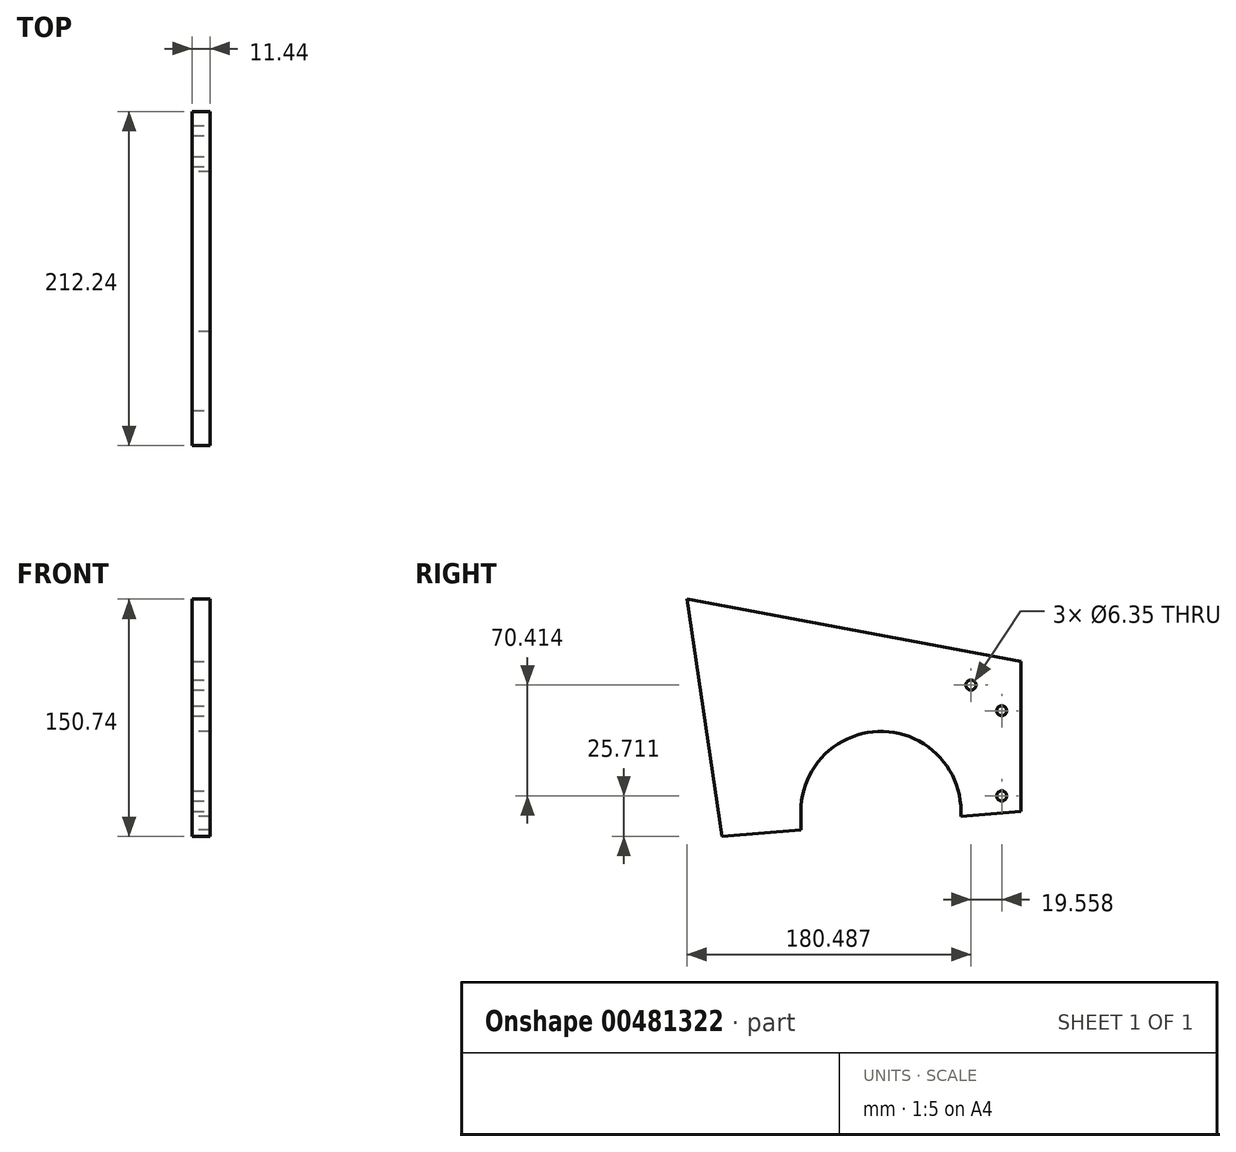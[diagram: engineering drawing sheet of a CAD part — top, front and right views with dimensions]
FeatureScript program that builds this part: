
annotation { "Feature Type Name" : "Feature", "Feature Type Description" : "" }
export const myFeature = defineFeature(function(context is Context, id is Id, definition is map)
    precondition{}
    {
        {
            var Q0;
            Q0=qCreatedBy(makeId("Right.planeOp"),FACE);
            var sketch = newSketch(context, id + "F0", { "sketchPlane" : qUnion([Q0])});
            skLineSegment(sketch, "E0", {"start": v(122.12, 51.37) * mm, "end": v(-90.12, 90.98) * mm});
            skLineSegment(sketch, "E1", {"start": v(-90.12, 90.98) * mm, "end": v(-67.72, -59.76) * mm});
            skLineSegment(sketch, "E2", {"start": v(122.12, 51.37) * mm, "end": v(122.12, -43.88) * mm});
            skLineSegment(sketch, "E3", {"start": v(-67.72, -59.76) * mm, "end": v(122.12, -43.88) * mm});
            skCircle(sketch, "E4", {"center": v(90.37, 36.36) * mm, "radius": 3.18 * mm});
            skCircle(sketch, "E5", {"center": v(109.92, 20.05) * mm, "radius": 3.18 * mm});
            skCircle(sketch, "E6", {"center": v(109.92, -34.05) * mm, "radius": 3.18 * mm});
            skSolve(sketch);
        }
        {
            var Q0;
            Q0=qSketchRegion(id+"F0",true);
            var Q1;
            Q1=makeQuery(id+"F0.imprint","IMPRINT",FACE,{"disambiguationData":[TD([[makeQuery(id+"F0.imprint","IMPRINT",EDGE,{"derivedFrom":sQuery(id+"F0.wireOp",EDGE,"E4")}),1.0]])]});
            var Q2;
            Q2=makeQuery(id+"F0.imprint","IMPRINT",FACE,{"disambiguationData":[TD([[makeQuery(id+"F0.imprint","IMPRINT",EDGE,{"derivedFrom":sQuery(id+"F0.wireOp",EDGE,"E5")}),1.0]])]});
            var Q3;
            Q3=makeQuery(id+"F0.imprint","IMPRINT",FACE,{"disambiguationData":[TD([[makeQuery(id+"F0.imprint","IMPRINT",EDGE,{"derivedFrom":sQuery(id+"F0.wireOp",EDGE,"E6")}),1.0]])]});
            extrude(context, id + "F1", {"entities" : qUnion([Q0, Q1, Q2, Q3]), "depth" : 11.43 * mm});
        }
        {
            var Q0;
            Q0=makeQuery(id+"F1.opExtrude","SWEPT_BODY",BODY,{"disambiguationData":[OSD([sQuery(id+"F0.wireOp",EDGE,"E0"),sQuery(id+"F0.wireOp",EDGE,"E1"),sQuery(id+"F0.wireOp",EDGE,"E2"),sQuery(id+"F0.wireOp",EDGE,"E3"),sQuery(id+"F0.wireOp",EDGE,"E4"),sQuery(id+"F0.wireOp",EDGE,"E5"),sQuery(id+"F0.wireOp",EDGE,"E6")])]});
            transform(context, id + "F2", {"entities" : qUnion([Q0]), "transformType" : TransformType.TRANSLATION_3D, "dx" : 47.62 * mm, "dy" : 0 * mm, "dz" : 0 * mm, "makeCopy" : false});
        }
        {
            var Q0;
            Q0=makeQuery(id+"F1.opExtrude","SWEPT_BODY",BODY,{"disambiguationData":[OSD([sQuery(id+"F0.wireOp",EDGE,"E0"),sQuery(id+"F0.wireOp",EDGE,"E1"),sQuery(id+"F0.wireOp",EDGE,"E2"),sQuery(id+"F0.wireOp",EDGE,"E3"),sQuery(id+"F0.wireOp",EDGE,"E4"),sQuery(id+"F0.wireOp",EDGE,"E5"),sQuery(id+"F0.wireOp",EDGE,"E6")])]});
            var Q1;
            Q1=qCreatedBy(makeId("Right.planeOp"),FACE);
            mirror(context, id + "F3", {"entities" : qUnion([Q0]), "mirrorPlane" : qUnion([Q1])});
        }
        {
            var Q0;
            Q0=makeQuery(id+"F3.opPattern","COPY",FACE,{"derivedFrom":makeQuery(id+"F1.opExtrude","CAP_FACE",FACE,{"disambiguationData":[OSD([sQuery(id+"F0.wireOp",EDGE,"E0"),sQuery(id+"F0.wireOp",EDGE,"E1"),sQuery(id+"F0.wireOp",EDGE,"E2"),sQuery(id+"F0.wireOp",EDGE,"E3"),sQuery(id+"F0.wireOp",EDGE,"E4"),sQuery(id+"F0.wireOp",EDGE,"E5"),sQuery(id+"F0.wireOp",EDGE,"E6")])],"isStart":false}),"instanceName":"1"});
            var sketch = newSketch(context, id + "F4", { "sketchPlane" : qUnion([Q0])});
            skLineSegment(sketch, "E7", {"start": v(-122.12, -43.88) * mm, "end": v(-33.22, -43.88) * mm});
            skCircle(sketch, "E8", {"center": v(-33.22, -43.88) * mm, "radius": 50.8 * mm});
            skLineSegment(sketch, "E9", {"start": v(17.58, -43.88) * mm, "end": v(17.58, -55.57) * mm});
            skSolve(sketch);
        }
        {
            var Q0;
            {var subQ0=sQuery(id+"F4.wireOp",EDGE,"E8");var subQ1=makeQuery(id+"F4.imprint","INTERSECT",VERTEX,{"derivedFrom":[subQ0,sQuery(id+"F4.wireOp",EDGE,"E9")]});Q0=makeQuery(id+"F4.imprint","IMPRINT",FACE,{"disambiguationData":[TD([[makeQuery(id+"F4.imprint","IMPRINT",EDGE,{"disambiguationData":[TD([[subQ1,-1.0]])],"derivedFrom":subQ0}),1.0]])]});}
            var Q1;
            {var subQ0=sQuery(id+"F4.wireOp",EDGE,"E9");Q1=makeQuery(id+"F4.imprint","IMPRINT",FACE,{"disambiguationData":[TD([[makeQuery(id+"F4.imprint","IMPRINT",EDGE,{"derivedFrom":subQ0}),-1.0]])]});}
            extrude(context, id + "F5", {"entities" : qUnion([Q0, Q1]), "operationType" : NewBodyOperationType.REMOVE, "oppositeDirection" : true, "depth" : 25.4 * mm});
        }
        {
            var Q0;
            Q0=sQuery(id+"F0.wireOp",VERTEX,"E4.center");
            var Q1;
            Q1=makeQuery(id+"F3.opPattern","COPY",BODY,{"derivedFrom":makeQuery(id+"F1.opExtrude","SWEPT_BODY",BODY,{"disambiguationData":[OSD([sQuery(id+"F0.wireOp",EDGE,"E0"),sQuery(id+"F0.wireOp",EDGE,"E1"),sQuery(id+"F0.wireOp",EDGE,"E2"),sQuery(id+"F0.wireOp",EDGE,"E3")])]}),"instanceName":"1"});
            hole(context, id + "F6", {"style" : HoleStyle.SIMPLE, "endStyle" : HoleEndStyle.BLIND, "holeDiameter" : 6.35 * mm, "holeDepth" : 76.2 * mm, "isTappedThrough" : true, "tappedDepth" : 12.7 * mm, "tapClearance" : 3, "startFromSketch" : true, "locations" : qUnion([Q0]), "scope" : qUnion([Q1])});
        }
        {
            var Q0;
            Q0=sQuery(id+"F0.wireOp",VERTEX,"E5.center");
            var Q1;
            Q1=makeQuery(id+"F3.opPattern","COPY",BODY,{"derivedFrom":makeQuery(id+"F1.opExtrude","SWEPT_BODY",BODY,{"disambiguationData":[OSD([sQuery(id+"F0.wireOp",EDGE,"E0"),sQuery(id+"F0.wireOp",EDGE,"E1"),sQuery(id+"F0.wireOp",EDGE,"E2"),sQuery(id+"F0.wireOp",EDGE,"E3")])]}),"instanceName":"1"});
            hole(context, id + "F7", {"style" : HoleStyle.SIMPLE, "endStyle" : HoleEndStyle.BLIND, "holeDiameter" : 6.35 * mm, "holeDepth" : 76.2 * mm, "isTappedThrough" : true, "tappedDepth" : 12.7 * mm, "tapClearance" : 3, "startFromSketch" : true, "locations" : qUnion([Q0]), "scope" : qUnion([Q1])});
        }
        {
            var Q0;
            Q0=sQuery(id+"F0.wireOp",VERTEX,"E6.center");
            var Q1;
            Q1=makeQuery(id+"F3.opPattern","COPY",BODY,{"derivedFrom":makeQuery(id+"F1.opExtrude","SWEPT_BODY",BODY,{"disambiguationData":[OSD([sQuery(id+"F0.wireOp",EDGE,"E0"),sQuery(id+"F0.wireOp",EDGE,"E1"),sQuery(id+"F0.wireOp",EDGE,"E2"),sQuery(id+"F0.wireOp",EDGE,"E3")])]}),"instanceName":"1"});
            hole(context, id + "F8", {"style" : HoleStyle.SIMPLE, "endStyle" : HoleEndStyle.BLIND, "holeDiameter" : 6.35 * mm, "holeDepth" : 76.2 * mm, "isTappedThrough" : true, "tappedDepth" : 12.7 * mm, "tapClearance" : 3, "startFromSketch" : true, "locations" : qUnion([Q0]), "scope" : qUnion([Q1])});
        }
        {
            var Q0;
            Q0=sQuery(id+"F0.wireOp",VERTEX,"E4.center");
            var Q1;
            Q1=makeQuery(id+"F1.opExtrude","SWEPT_BODY",BODY,{"disambiguationData":[OSD([sQuery(id+"F0.wireOp",EDGE,"E0"),sQuery(id+"F0.wireOp",EDGE,"E1"),sQuery(id+"F0.wireOp",EDGE,"E2"),sQuery(id+"F0.wireOp",EDGE,"E3")])]});
            hole(context, id + "F9", {"style" : HoleStyle.SIMPLE, "endStyle" : HoleEndStyle.BLIND, "oppositeDirection" : true, "holeDiameter" : 6.35 * mm, "holeDepth" : 76.2 * mm, "isTappedThrough" : true, "tappedDepth" : 12.7 * mm, "tapClearance" : 3, "startFromSketch" : true, "locations" : qUnion([Q0]), "scope" : qUnion([Q1])});
        }
        {
            var Q0;
            Q0=makeQuery(id+"F1.opExtrude","CAP_FACE",FACE,{"disambiguationData":[OSD([sQuery(id+"F0.wireOp",EDGE,"E0"),sQuery(id+"F0.wireOp",EDGE,"E1"),sQuery(id+"F0.wireOp",EDGE,"E2"),sQuery(id+"F0.wireOp",EDGE,"E3")])],"isStart":true});
            var sketch = newSketch(context, id + "F10", { "sketchPlane" : qUnion([Q0])});
            skCircle(sketch, "E10", {"center": v(-90.37, 36.36) * mm, "radius": 66.68 * mm});
            skCircle(sketch, "E11.0", {"center": v(-90.37, 36.36) * mm, "radius": 161.93 * mm});
            skCircle(sketch, "E12.0", {"center": v(-90.37, 36.36) * mm, "radius": 164.47 * mm});
            skLineSegment(sketch, "E13", {"start": v(52.96, -38.98) * mm, "end": v(55.23, -40.13) * mm});
            skLineSegment(sketch, "E14", {"start": v(66.26, 86.53) * mm, "end": v(48.44, 142.17) * mm});
            skLineSegment(sketch, "E15", {"start": v(48.44, 142.17) * mm, "end": v(46.02, 141.4) * mm});
            skLineSegment(sketch, "E16", {"start": v(46.02, 141.4) * mm, "end": v(63.74, 86.06) * mm});
            skSolve(sketch);
        }
        {
            var Q0;
            {var subQ0=sQuery(id+"F10.wireOp",EDGE,"E14");Q0=makeQuery(id+"F10.imprint","IMPRINT",FACE,{"disambiguationData":[TD([[makeQuery(id+"F10.imprint","IMPRINT",EDGE,{"derivedFrom":subQ0}),1.0]])]});}
            var Q1;
            {var subQ1=makeQuery(id+"F1.opExtrude","CAP_EDGE",EDGE,{"disambiguationData":[OSD([sQuery(id+"F0.wireOp",EDGE,"E0")])],"isStart":true});var subQ3=sQuery(id+"F10.wireOp",EDGE,"E16");var subQ5=makeQuery(id+"F10.imprint","INTERSECT",VERTEX,{"derivedFrom":[subQ1,subQ3]});Q1=makeQuery(id+"F10.imprint","IMPRINT",FACE,{"disambiguationData":[TD([[makeQuery(id+"F10.imprint","IMPRINT",EDGE,{"disambiguationData":[TD([[subQ5,1.0]])],"derivedFrom":subQ3}),1.0]])]});}
            var Q2;
            {var subQ4=sQuery(id+"F10.wireOp",EDGE,"E13");Q2=makeQuery(id+"F10.imprint","IMPRINT",FACE,{"disambiguationData":[TD([[makeQuery(id+"F10.imprint","IMPRINT",EDGE,{"derivedFrom":subQ4}),1.0]])]});}
            extrude(context, id + "F11", {"entities" : qUnion([Q0, Q1, Q2]), "depth" : 95.25 * mm});
        }
        {
            var Q0;
            Q0=makeQuery(id+"F1.opExtrude","SWEPT_BODY",BODY,{"disambiguationData":[OSD([sQuery(id+"F0.wireOp",EDGE,"E0"),sQuery(id+"F0.wireOp",EDGE,"E1"),sQuery(id+"F0.wireOp",EDGE,"E2"),sQuery(id+"F0.wireOp",EDGE,"E3")])]});
            deleteBodies(context, id + "F12", {"entities" : qUnion([Q0])});
        }
        {
            var Q0;
            Q0=makeQuery(id+"F1.opExtrude","SWEPT_BODY",BODY,{"disambiguationData":[OSD([sQuery(id+"F0.wireOp",EDGE,"E0"),sQuery(id+"F0.wireOp",EDGE,"E1"),sQuery(id+"F0.wireOp",EDGE,"E2"),sQuery(id+"F0.wireOp",EDGE,"E3")])]});
            var Q1;
            Q1=makeQuery(id+"F11.opExtrude","SWEPT_BODY",BODY,{"disambiguationData":[OSD([sQuery(id+"F0.wireOp",EDGE,"E0"),sQuery(id+"F10.wireOp",EDGE,"E11.0"),sQuery(id+"F10.wireOp",EDGE,"E12.0"),sQuery(id+"F10.wireOp",EDGE,"E13"),sQuery(id+"F10.wireOp",EDGE,"E14"),sQuery(id+"F10.wireOp",EDGE,"E15"),sQuery(id+"F10.wireOp",EDGE,"E16")])]});
            deleteBodies(context, id + "F13", {"entities" : qUnion([Q0, Q1])});
        }
    });
